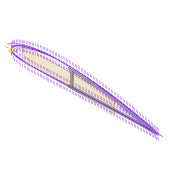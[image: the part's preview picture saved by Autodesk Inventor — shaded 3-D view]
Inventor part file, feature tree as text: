
AUTODESK INVENTOR PART (.ipt)
format: ipt  version: 2022 (Build 260153000, 153)  size: 371,712 bytes
history: native  units: mm
features: extrude x7, sketch x7, projected_geometry x5, shell x1, fillet x1, plane x1
ambient origin geometry x8: Origin, YZ Plane, XZ Plane, XY Plane, X Axis, Y Axis, Z Axis, Center Point
bodies: Solid1 (feature_tree)
feature tree (22):
  extrude  "Extrusion1"  Depth=5.0mm
  shell  "Shell1"  Thickness=2.0mm
  extrude  "Extrusion8"  Depth=5.9mm
  extrude  "Extrusion3"  Depth=10.0mm TaperAngle=0.0deg
  extrude  "Extrusion4"  Depth=2.0mm
  fillet  "Fillet1"  Radius=5.0mm
  extrude  "Extrusion5"  Depth=2.5mm
  plane  "Work Plane2"
  extrude  "Extrusion9"  Depth=1.6mm
  extrude  "Extrusion10"  Depth=77.0mm
  sketch  "Sketch3"  dims[d0=4.0mm d1=0.0mm d2=5.0mm d7=2.0mm]
  sketch  "Sketch8"  dims[d8=2.0mm d9=5.9mm]
  sketch  "Sketch9"  dims[d13=10.0mm d14=0.0mm d16=10.0mm d17=0.0mm]
  sketch  "Sketch10"  dims[d22=4.0mm d23=0.0mm d31=2.0mm d32=5.0mm]
  projected_geometry  "Projected Loop4"
  projected_geometry  "Projected Loop10"
  sketch  "Sketch24"  dims[d34=1.6mm d35=2.5mm]
  projected_geometry  "Projected Loop11"
  projected_geometry  "Projected Loop12"
  sketch  "Sketch26"  dims[d37=5.0mm d38=1.6mm]
  projected_geometry  "Projected Loop13"
  sketch  "Sketch27"  dims[d40=2.5mm d62=77.0mm d63=6.0mm d64=4.0mm d65=0.0mm d66=3.0mm d67=12.0mm d68=80.0mm d69=20.0mm d70=0.5mm d71=10.0mm d72=0.0mm d73=10.0mm d74=0.0mm]
